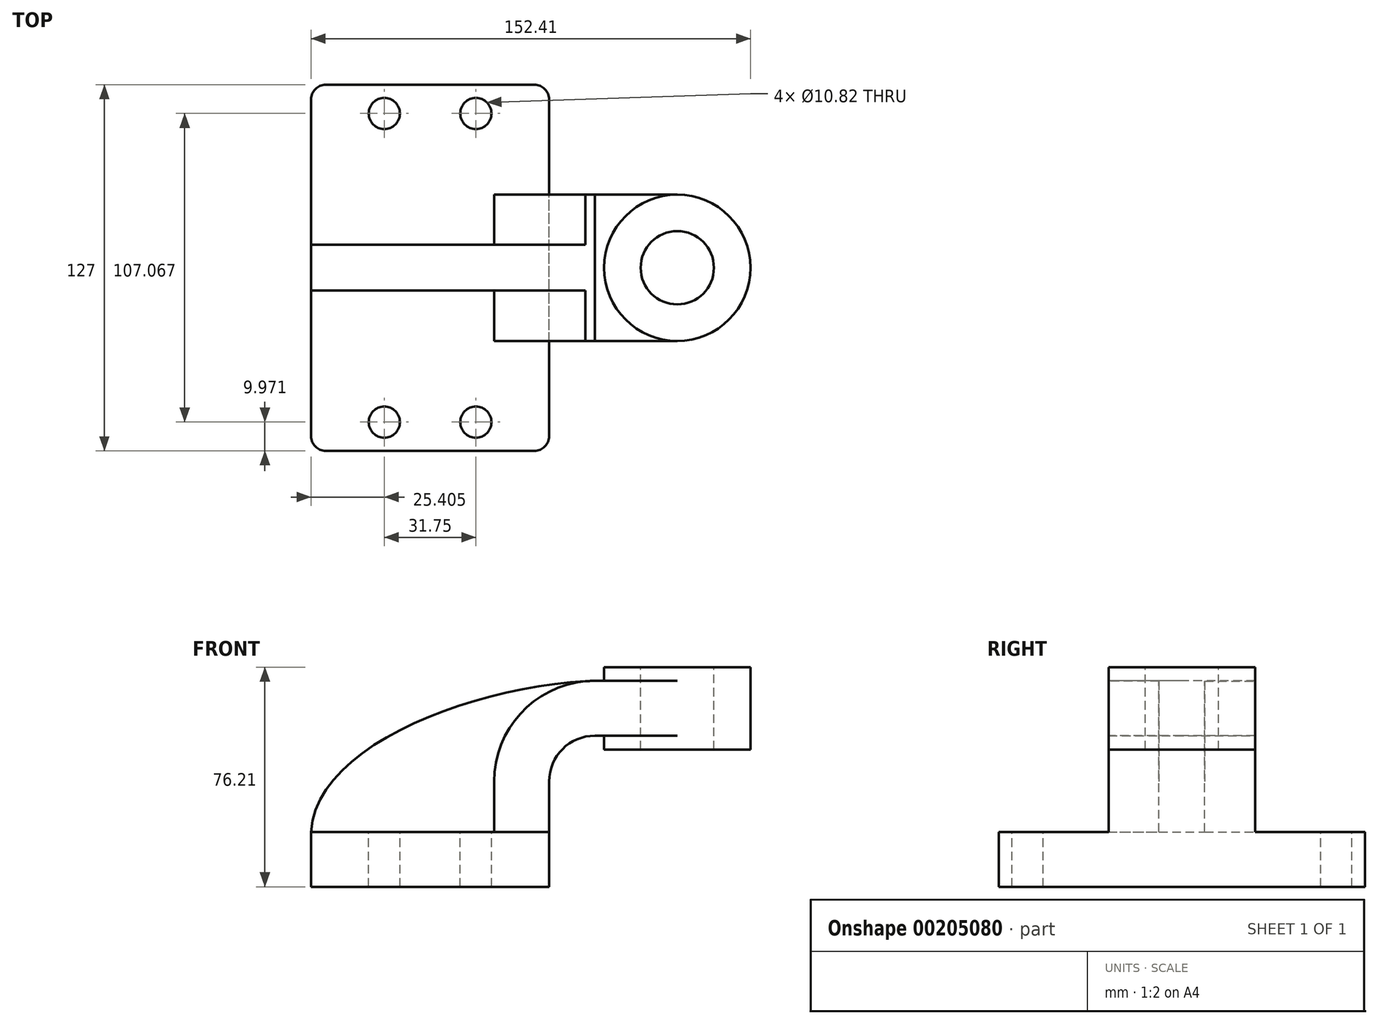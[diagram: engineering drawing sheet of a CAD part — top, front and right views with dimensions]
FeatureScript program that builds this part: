
annotation { "Feature Type Name" : "Feature", "Feature Type Description" : "" }
export const myFeature = defineFeature(function(context is Context, id is Id, definition is map)
    precondition{}
    {
        {
            var Q0;
            Q0=qCreatedBy(makeId("Front.planeOp"),FACE);
            var sketch = newSketch(context, id + "F0", { "sketchPlane" : qUnion([Q0])});
            skLineSegment(sketch, "E0.rect.bottom", {"start": v(-41.28, 9.52) * mm, "end": v(41.28, 9.52) * mm});
            skLineSegment(sketch, "E0.rect.top", {"start": v(-41.28, -9.52) * mm, "end": v(41.28, -9.52) * mm});
            skLineSegment(sketch, "E0.rect.left", {"start": v(-41.28, 9.52) * mm, "end": v(-41.28, -9.52) * mm});
            skLineSegment(sketch, "E0.rect.right", {"start": v(41.28, 9.52) * mm, "end": v(41.28, -9.52) * mm});
            skPoint(sketch, "E0.rect.middle", {"position": v(0, 0) * mm});
            skLineSegment(sketch, "E1", {"start": v(41.28, 9.52) * mm, "end": v(41.28, 27) * mm});
            skArc(sketch, "E2", {"start": v(41.28, 27) * mm, "mid": v(45.92, 38.23) * mm, "end": v(57.15, 42.88) * mm});
            skLineSegment(sketch, "E3", {"start": v(57.15, 42.88) * mm, "end": v(85.72, 42.88) * mm});
            skLineSegment(sketch, "E4.rect.bottom", {"start": v(60.32, 38.1) * mm, "end": v(111.12, 38.1) * mm});
            skLineSegment(sketch, "E4.rect.top", {"start": v(60.32, 66.68) * mm, "end": v(111.12, 66.68) * mm});
            skLineSegment(sketch, "E4.rect.left", {"start": v(60.32, 38.1) * mm, "end": v(60.32, 66.68) * mm});
            skLineSegment(sketch, "E4.rect.right", {"start": v(111.13, 38.1) * mm, "end": v(111.12, 66.68) * mm});
            skPoint(sketch, "E4.rect.middle", {"position": v(85.72, 52.39) * mm});
            skLineSegment(sketch, "E5.0", {"start": v(57.15, 61.93) * mm, "end": v(85.72, 61.93) * mm});
            skArc(sketch, "E5.1", {"start": v(22.23, 27) * mm, "mid": v(32.45, 51.7) * mm, "end": v(57.15, 61.93) * mm});
            skLineSegment(sketch, "E5.2", {"start": v(22.23, 9.52) * mm, "end": v(22.23, 27) * mm});
            skLineSegment(sketch, "E6", {"start": v(85.72, 38.1) * mm, "end": v(85.72, 66.68) * mm});
            skFitSpline(sketch, "E7", {"points": [v(-41.28, 9.53) * mm, v(57.15, 61.93) * mm], "startDerivative": vector(5.2, 92.34) * mm, "endDerivative": vector(120.92, 4.22) * mm});
            skSolve(sketch);
        }
        {
            var Q0;
            Q0=makeQuery(id+"F0.imprint","IMPRINT",FACE,{"disambiguationData":[TD([[makeQuery(id+"F0.imprint","IMPRINT",EDGE,{"derivedFrom":sQuery(id+"F0.wireOp",EDGE,"E0.rect.top")}),1.0]])]});
            extrude(context, id + "F1", {"entities" : qUnion([Q0]), "endBound" : BoundingType.SYMMETRIC, "depth" : 127 * mm});
        }
        {
            var Q0;
            {var subQ9=sQuery(id+"F0.wireOp",EDGE,"E1");Q0=makeQuery(id+"F0.imprint","IMPRINT",FACE,{"disambiguationData":[TD([[makeQuery(id+"F0.imprint","IMPRINT",EDGE,{"derivedFrom":subQ9}),1.0]])]});}
            var Q1;
            {var subQ0=sQuery(id+"F0.wireOp",EDGE,"E6");var subQ1=sQuery(id+"F0.wireOp",EDGE,"E3");var subQ2=makeQuery(id+"F0.imprint","INTERSECT",VERTEX,{"derivedFrom":[subQ1,subQ0]});Q1=makeQuery(id+"F0.imprint","IMPRINT",FACE,{"disambiguationData":[TD([[makeQuery(id+"F0.imprint","IMPRINT",EDGE,{"disambiguationData":[TD([[subQ2,1.0]])],"derivedFrom":subQ1}),1.0]])]});}
            extrude(context, id + "F2", {"entities" : qUnion([Q0, Q1]), "operationType" : NewBodyOperationType.ADD, "endBound" : BoundingType.SYMMETRIC, "depth" : 50.8 * mm});
        }
        {
            var Q0;
            {var subQ3=sQuery(id+"F0.wireOp",EDGE,"E5.2");Q0=makeQuery(id+"F0.imprint","IMPRINT",FACE,{"disambiguationData":[TD([[makeQuery(id+"F0.imprint","IMPRINT",EDGE,{"derivedFrom":subQ3}),1.0]])]});}
            extrude(context, id + "F3", {"entities" : qUnion([Q0]), "operationType" : NewBodyOperationType.ADD, "endBound" : BoundingType.SYMMETRIC, "depth" : 15.88 * mm});
        }
        {
            var Q0;
            {var subQ5=sQuery(id+"F0.wireOp",EDGE,"E4.rect.right");Q0=makeQuery(id+"F0.imprint","IMPRINT",FACE,{"disambiguationData":[TD([[makeQuery(id+"F0.imprint","IMPRINT",EDGE,{"derivedFrom":subQ5}),1.0]])]});}
            var Q1;
            Q1=sQuery(id+"F0.wireOp",EDGE,"E6");
            revolve(context, id + "F4", {"operationType" : NewBodyOperationType.ADD, "entities" : qUnion([Q0]), "axis" : qUnion([Q1]), "revolveType" : RevolveType.FULL});
        }
        {
            var Q0;
            Q0=makeQuery(id+"F1.opExtrude","CAP_EDGE",EDGE,{"disambiguationData":[OSD([sQuery(id+"F0.wireOp",EDGE,"E0.rect.right")])],"isStart":false});
            var Q1;
            Q1=makeQuery(id+"F1.opExtrude","CAP_EDGE",EDGE,{"disambiguationData":[OSD([sQuery(id+"F0.wireOp",EDGE,"E0.rect.left")])],"isStart":false});
            var Q2;
            Q2=makeQuery(id+"F1.opExtrude","CAP_EDGE",EDGE,{"disambiguationData":[OSD([sQuery(id+"F0.wireOp",EDGE,"E0.rect.right")])],"isStart":true});
            var Q3;
            Q3=makeQuery(id+"F1.opExtrude","CAP_EDGE",EDGE,{"disambiguationData":[OSD([sQuery(id+"F0.wireOp",EDGE,"E0.rect.left")])],"isStart":true});
            fillet(context, id + "F5", {"entities" : qUnion([Q0, Q1, Q2, Q3]), "radius" : 5.08 * mm, "tangentPropagation" : true, "allowEdgeOverflow" : false});
        }
        {
            var Q0;
            Q0=makeQuery(id+"F4.opRevolve","SWEPT_FACE",FACE,{"disambiguationData":[OSD([sQuery(id+"F0.wireOp",EDGE,"E4.rect.top")])]});
            var sketch = newSketch(context, id + "F6", { "sketchPlane" : qUnion([Q0])});
            skCircle(sketch, "E8", {"center": v(85.72, 0) * mm, "radius": 12.8 * mm});
            skSolve(sketch);
        }
        {
            var Q0;
            {var subQ4=sQuery(id+"F0.wireOp",EDGE,"E0.rect.bottom");var subQ5=sQuery(id+"F0.wireOp",EDGE,"E0.rect.right");var subQ6=sQuery(id+"F0.wireOp",EDGE,"E0.rect.left");Q0=makeQuery(id+"F3.boolean.opBoolean","SPLIT",FACE,{"disambiguationData":[TD([makeQuery(id+"F1.opExtrude","CAP_FACE",FACE,{"disambiguationData":[OSD([subQ4,sQuery(id+"F0.wireOp",EDGE,"E0.rect.top"),subQ6,subQ5])],"isStart":true})])],"derivedFrom":makeQuery(id+"F1.opExtrude","SWEPT_FACE",FACE,{"disambiguationData":[OSD([subQ4])]})});}
            var sketch = newSketch(context, id + "F7", { "sketchPlane" : qUnion([Q0])});
            skCircle(sketch, "E9", {"center": v(-15.88, 53.54) * mm, "radius": 5.41 * mm});
            skCircle(sketch, "E10", {"center": v(15.88, 53.54) * mm, "radius": 5.41 * mm});
            skSolve(sketch);
        }
        {
            var Q0;
            {var subQ4=sQuery(id+"F0.wireOp",EDGE,"E0.rect.bottom");var subQ5=sQuery(id+"F0.wireOp",EDGE,"E0.rect.right");var subQ6=sQuery(id+"F0.wireOp",EDGE,"E0.rect.left");Q0=makeQuery(id+"F3.boolean.opBoolean","SPLIT",FACE,{"disambiguationData":[TD([makeQuery(id+"F1.opExtrude","CAP_FACE",FACE,{"disambiguationData":[OSD([subQ4,sQuery(id+"F0.wireOp",EDGE,"E0.rect.top"),subQ6,subQ5])],"isStart":false})])],"derivedFrom":makeQuery(id+"F1.opExtrude","SWEPT_FACE",FACE,{"disambiguationData":[OSD([subQ4])]})});}
            var sketch = newSketch(context, id + "F8", { "sketchPlane" : qUnion([Q0])});
            skCircle(sketch, "E11", {"center": v(-15.88, -53.53) * mm, "radius": 5.41 * mm});
            skCircle(sketch, "E12", {"center": v(15.88, -53.53) * mm, "radius": 5.41 * mm});
            skSolve(sketch);
        }
        {
            var Q0;
            Q0=sQuery(id+"F7.wireOp",VERTEX,"E9.center");
            var Q1;
            Q1=sQuery(id+"F7.wireOp",VERTEX,"E10.center");
            var Q2;
            Q2=makeQuery(id+"F1.opExtrude","SWEPT_BODY",BODY,{"disambiguationData":[OSD([sQuery(id+"F0.wireOp",EDGE,"E0.rect.bottom"),sQuery(id+"F0.wireOp",EDGE,"E0.rect.top"),sQuery(id+"F0.wireOp",EDGE,"E0.rect.left"),sQuery(id+"F0.wireOp",EDGE,"E0.rect.right")])]});
            hole(context, id + "F9", {"style" : HoleStyle.SIMPLE, "endStyle" : HoleEndStyle.THROUGH, "holeDiameter" : 10.82 * mm, "locations" : qUnion([Q0, Q1]), "scope" : qUnion([Q2]), "isTappedThrough" : true});
        }
        {
            var Q0;
            Q0=sQuery(id+"F8.wireOp",VERTEX,"E11.center");
            var Q1;
            Q1=sQuery(id+"F8.wireOp",VERTEX,"E12.center");
            var Q2;
            Q2=makeQuery(id+"F1.opExtrude","SWEPT_BODY",BODY,{"disambiguationData":[OSD([sQuery(id+"F0.wireOp",EDGE,"E0.rect.bottom"),sQuery(id+"F0.wireOp",EDGE,"E0.rect.top"),sQuery(id+"F0.wireOp",EDGE,"E0.rect.left"),sQuery(id+"F0.wireOp",EDGE,"E0.rect.right")])]});
            hole(context, id + "F10", {"style" : HoleStyle.SIMPLE, "endStyle" : HoleEndStyle.THROUGH, "holeDiameter" : 10.82 * mm, "locations" : qUnion([Q0, Q1]), "scope" : qUnion([Q2]), "isTappedThrough" : true});
        }
        {
            var Q0;
            Q0=sQuery(id+"F6.wireOp",VERTEX,"E8.center");
            var Q1;
            Q1=makeQuery(id+"F1.opExtrude","SWEPT_BODY",BODY,{"disambiguationData":[OSD([sQuery(id+"F0.wireOp",EDGE,"E0.rect.bottom"),sQuery(id+"F0.wireOp",EDGE,"E0.rect.top"),sQuery(id+"F0.wireOp",EDGE,"E0.rect.left"),sQuery(id+"F0.wireOp",EDGE,"E0.rect.right")])]});
            hole(context, id + "F11", {"style" : HoleStyle.SIMPLE, "endStyle" : HoleEndStyle.THROUGH, "holeDiameter" : 25.4 * mm, "locations" : qUnion([Q0]), "scope" : qUnion([Q1]), "isTappedThrough" : true});
        }
    });
